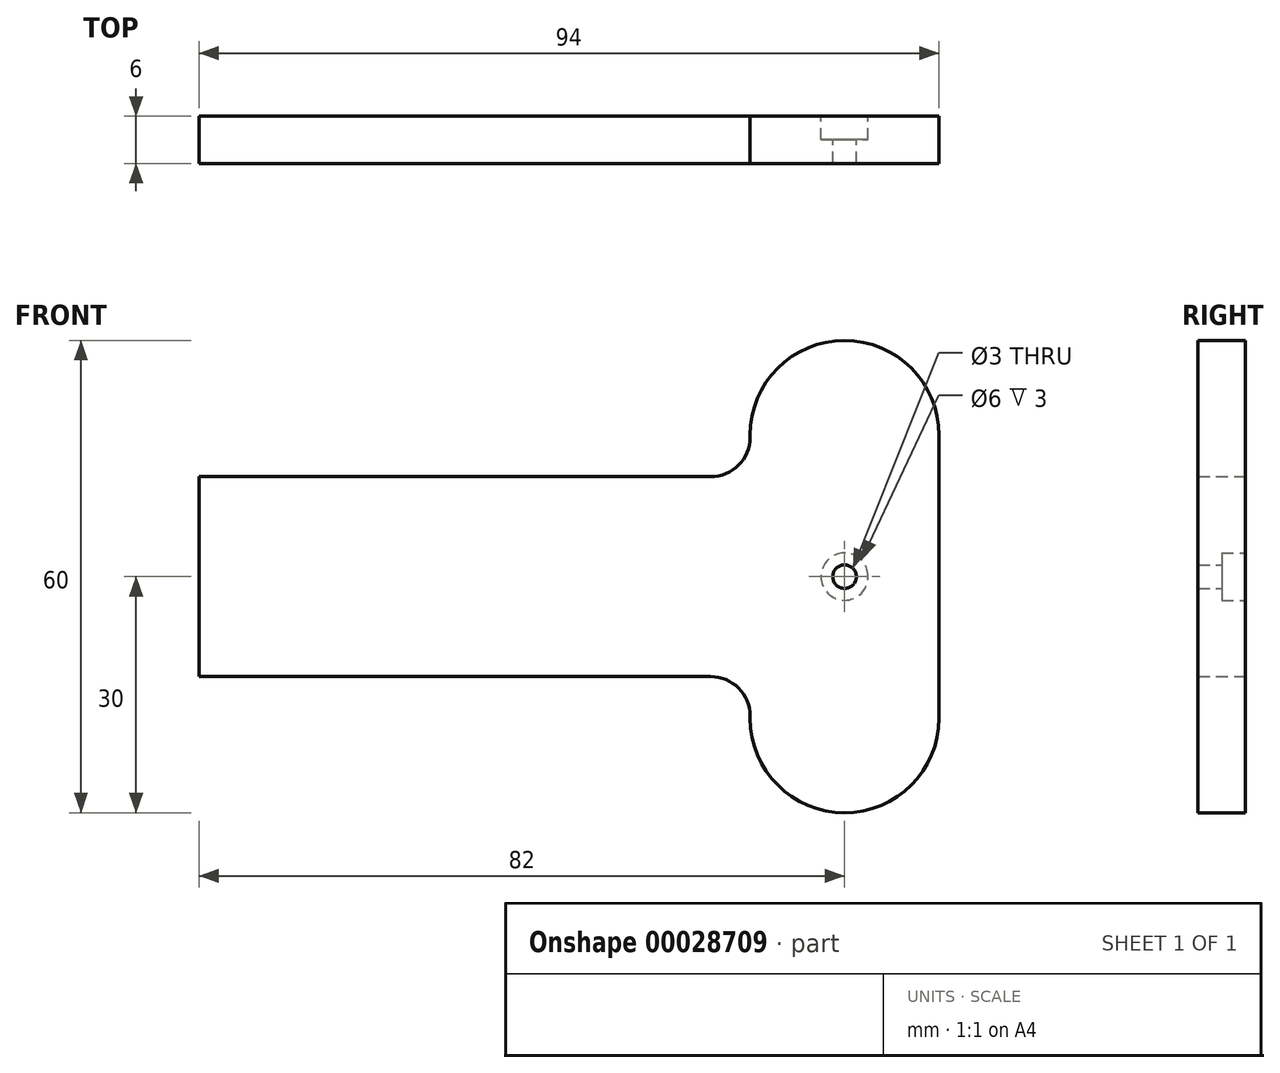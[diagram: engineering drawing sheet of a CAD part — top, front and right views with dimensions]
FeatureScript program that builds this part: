
annotation { "Feature Type Name" : "Feature", "Feature Type Description" : "" }
export const myFeature = defineFeature(function(context is Context, id is Id, definition is map)
    precondition{}
    {
        {
            var Q0;
            Q0=qCreatedBy(makeId("Front.planeOp"),FACE);
            var sketch = newSketch(context, id + "F0", { "sketchPlane" : qUnion([Q0])});
            skLineSegment(sketch, "E0", {"start": v(0, 12.7) * mm, "end": v(0, -12.7) * mm});
            skLineSegment(sketch, "E1", {"start": v(0, -12.7) * mm, "end": v(70, -12.7) * mm});
            skLineSegment(sketch, "E2", {"start": v(70, -12.7) * mm, "end": v(70, -18) * mm});
            skLineSegment(sketch, "E3", {"start": v(0, 0) * mm, "end": v(94, 0) * mm, "construction": true});
            skArc(sketch, "E4", {"start": v(70, -18) * mm, "mid": v(82, -30) * mm, "end": v(94, -18) * mm});
            skLineSegment(sketch, "E5", {"start": v(94, -18) * mm, "end": v(94, 18) * mm});
            skArc(sketch, "E6.MirrorCS", {"start": v(70, 18) * mm, "mid": v(82, 30) * mm, "end": v(94, 18) * mm});
            skLineSegment(sketch, "E7.MirrorCS", {"start": v(0, 12.7) * mm, "end": v(70, 12.7) * mm});
            skLineSegment(sketch, "E8.MirrorCS", {"start": v(70, 12.7) * mm, "end": v(70, 18) * mm});
            skPoint(sketch, "E9", {"position": v(82, 0) * mm});
            skCircle(sketch, "E10", {"center": v(82, 0) * mm, "radius": 29 * mm, "construction": true});
            skCircle(sketch, "E11", {"center": v(15, 0) * mm, "radius": 8 * mm, "construction": true});
            skLineSegment(sketch, "E12", {"start": v(49, 12.7) * mm, "end": v(49, -12.7) * mm, "construction": true});
            skLineSegment(sketch, "E13", {"start": v(41, 12.7) * mm, "end": v(41, -12.7) * mm, "construction": true});
            skSolve(sketch);
        }
        {
            var Q0;
            Q0 = qSketchRegion(id + "F0", true);
            extrude(context, id + "F1", {"entities" : qUnion([Q0]), "depth" : 6 * mm});
        }
        {
            var Q0;
            Q0=sQuery(id+"F0.wireOp",VERTEX,"E9");
            var Q1;
            Q1=makeQuery(id+"F1.opExtrude","SWEPT_BODY",BODY,{"disambiguationData":[OSD([sQuery(id+"F0.wireOp",EDGE,"E0"),sQuery(id+"F0.wireOp",EDGE,"E1"),sQuery(id+"F0.wireOp",EDGE,"E2"),sQuery(id+"F0.wireOp",EDGE,"E4"),sQuery(id+"F0.wireOp",EDGE,"E5"),sQuery(id+"F0.wireOp",EDGE,"E6.MirrorCS"),sQuery(id+"F0.wireOp",EDGE,"E7.MirrorCS"),sQuery(id+"F0.wireOp",EDGE,"E8.MirrorCS")])]});
            hole(context, id + "F2", {"style" : HoleStyle.C_BORE, "holeDiameter" : 3 * mm, "cBoreDiameter" : 6 * mm, "cBoreDepth" : 3 * mm, "endStyle" : HoleEndStyle.BLIND, "oppositeDirection" : true, "holeDepth" : 20 * mm, "locations" : qUnion([Q0]), "scope" : qUnion([Q1])});
        }
        {
            var Q0;
            Q0=makeQuery(id+"F1.opExtrude","SWEPT_EDGE",EDGE,{"disambiguationData":[OSD([sQuery(id+"F0.wireOp",EDGE,"E1"),sQuery(id+"F0.wireOp",EDGE,"E2")])]});
            var Q1;
            Q1=makeQuery(id+"F1.opExtrude","SWEPT_EDGE",EDGE,{"disambiguationData":[OSD([sQuery(id+"F0.wireOp",EDGE,"E7.MirrorCS"),sQuery(id+"F0.wireOp",EDGE,"E8.MirrorCS")])]});
            fillet(context, id + "F3", {"entities" : qUnion([Q0, Q1]), "radius" : 5 * mm, "tangentPropagation" : true, "allowEdgeOverflow" : false});
        }
    });
